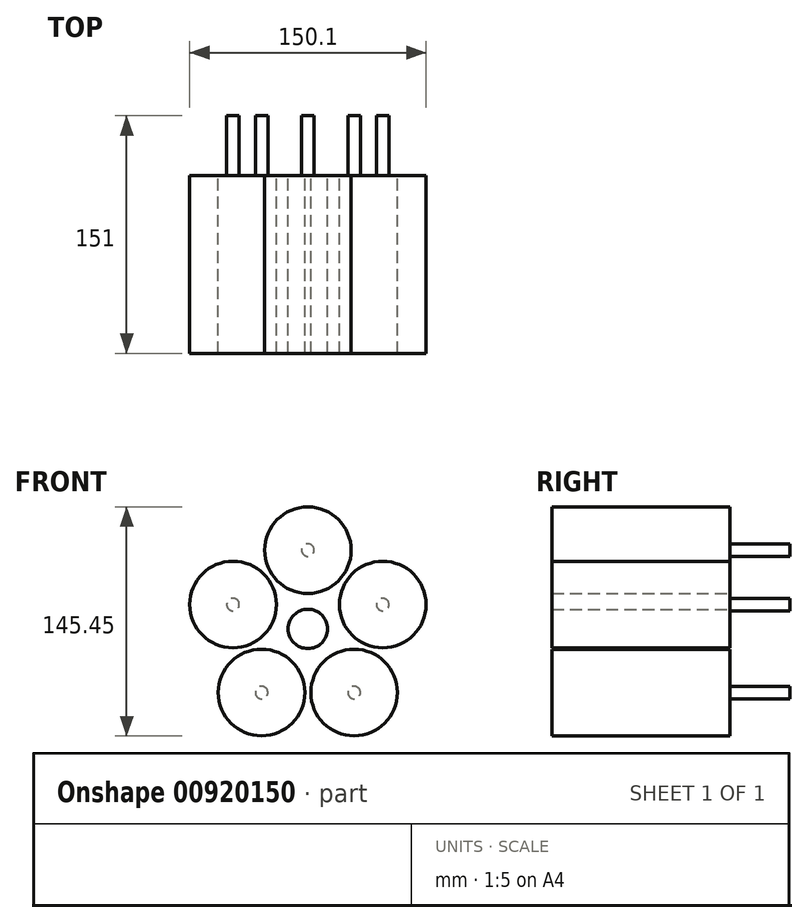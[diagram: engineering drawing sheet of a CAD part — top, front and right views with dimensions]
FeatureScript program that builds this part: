
annotation { "Feature Type Name" : "Feature", "Feature Type Description" : "" }
export const myFeature = defineFeature(function(context is Context, id is Id, definition is map)
    precondition{}
    {
        {
            var Q0;
            Q0=qCreatedBy(makeId("Front.planeOp"),FACE);
            var sketch = newSketch(context, id + "F0", { "sketchPlane" : qUnion([Q0])});
            skCircle(sketch, "E0", {"center": v(0, 0) * mm, "radius": 12.5 * mm});
            skCircle(sketch, "E1", {"center": v(0, 50) * mm, "radius": 27.5 * mm});
            skCircle(sketch, "E2", {"center": v(0, 0) * mm, "radius": 77.5 * mm, "construction": true});
            skCircle(sketch, "E3.1.0", {"center": v(-47.55, 15.45) * mm, "radius": 27.5 * mm});
            skCircle(sketch, "E3.2.0", {"center": v(-29.39, -40.45) * mm, "radius": 27.5 * mm});
            skCircle(sketch, "E3.3.0", {"center": v(29.39, -40.45) * mm, "radius": 27.5 * mm});
            skCircle(sketch, "E3.4.0", {"center": v(47.55, 15.45) * mm, "radius": 27.5 * mm});
            skSolve(sketch);
        }
        {
            var Q0;
            Q0 = qSketchRegion(id + "F0", true);
            extrude(context, id + "F1", {"entities" : qUnion([Q0]), "depth" : 113 * mm, "offsetDistance" : 25 * mm});
        }
        {
            var Q0;
            Q0=qCreatedBy(makeId("Front.planeOp"),FACE);
            var sketch = newSketch(context, id + "F2", { "sketchPlane" : qUnion([Q0])});
            skCircle(sketch, "E4", {"center": v(0, 50) * mm, "radius": 4 * mm});
            skCircle(sketch, "E5", {"center": v(47.55, 15.45) * mm, "radius": 4 * mm});
            skCircle(sketch, "E6", {"center": v(29.39, -40.45) * mm, "radius": 4 * mm});
            skCircle(sketch, "E7", {"center": v(-29.39, -40.45) * mm, "radius": 4 * mm});
            skCircle(sketch, "E8", {"center": v(-47.55, 15.45) * mm, "radius": 4 * mm});
            skSolve(sketch);
        }
        {
            var Q0;
            Q0 = qSketchRegion(id + "F2", true);
            extrude(context, id + "F3", {"entities" : qUnion([Q0]), "oppositeDirection" : true, "depth" : 38 * mm, "offsetDistance" : 25 * mm});
        }
    });
